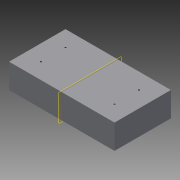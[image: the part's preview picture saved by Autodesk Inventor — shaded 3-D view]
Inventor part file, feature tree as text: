
AUTODESK INVENTOR PART (.ipt)
format: ipt  version: 2013 (Build 170138000, 138)  size: 87,552 bytes
history: native  units: mm
features: sketch x2, extrude x1, hole x1, plane x1
ambient origin geometry x8: Origin, YZ Plane, XZ Plane, XY Plane, X Axis, Y Axis, Z Axis, Center Point
bodies: Solid1 (feature_tree)
feature tree (5):
  extrude  "Extrusion1"  Depth=115.0mm
  hole  "Hole1"  [1 undecoded]
  plane  "Work Plane1"
  sketch  "Sketch1"  dims[d0=215.0mm d2=115.0mm]
  sketch  "Sketch2"  dims[d3=50.0mm d4=0.0mm d5=150.0mm d7=50.0mm d8=4.0mm d9=5.0mm d10=4.0mm d11=2.0mm d12=90.0deg d13=5.0mm d14=20.594885mm]
note: 1 required parameter value undecoded (feature->parameter linkage not recoverable at this tier; creation-order binding heuristic only, values carry confidence <= 0.55)
